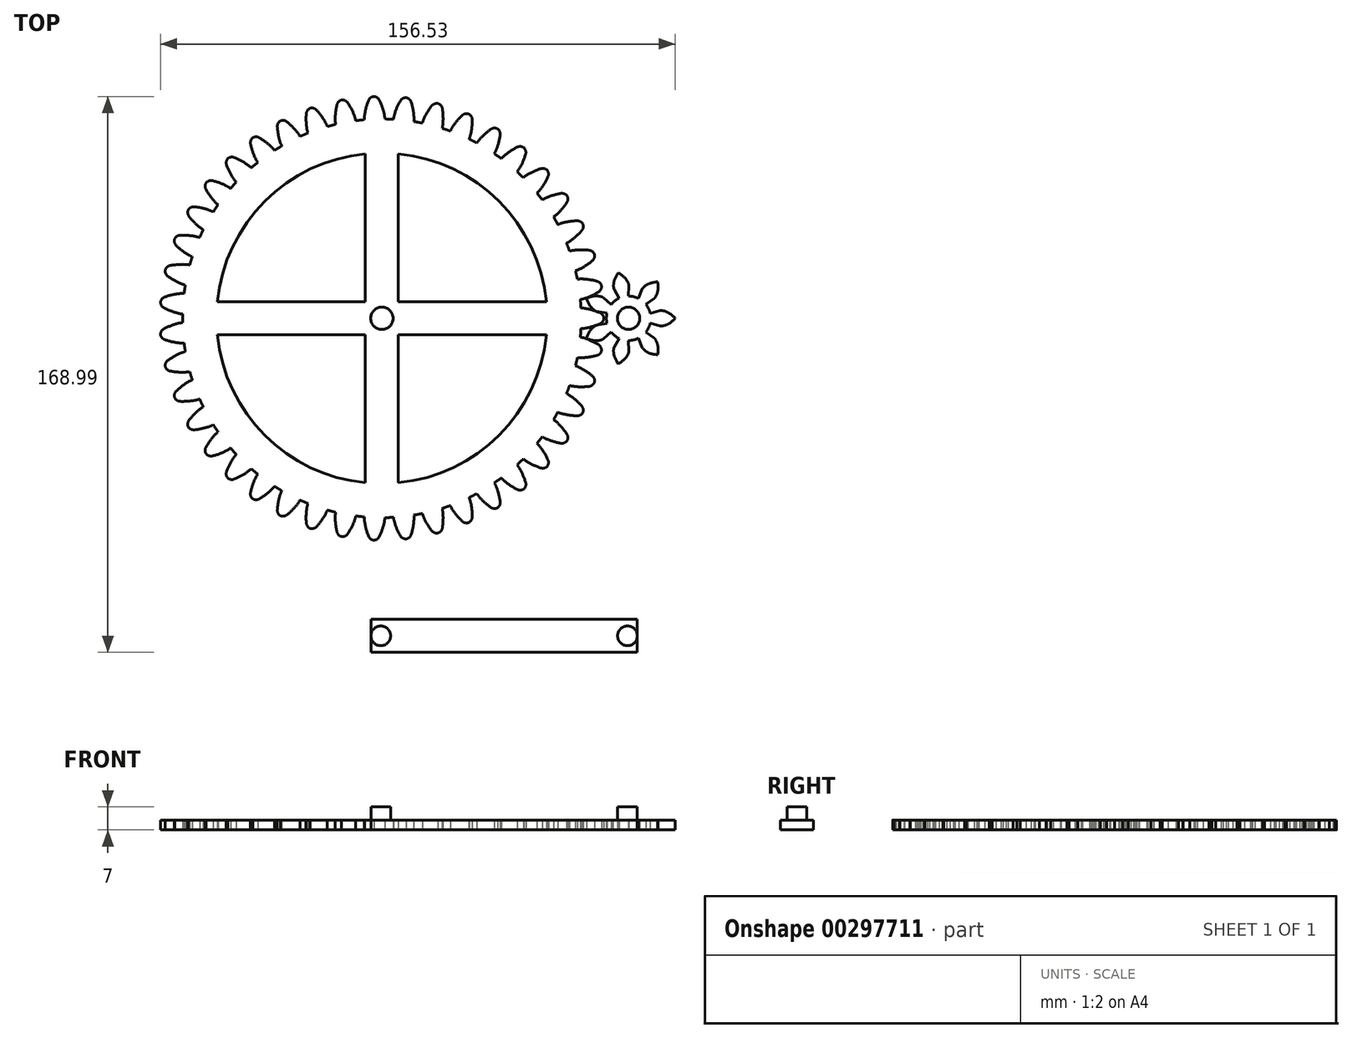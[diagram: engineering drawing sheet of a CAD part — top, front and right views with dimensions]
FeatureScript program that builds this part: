
annotation { "Feature Type Name" : "Feature", "Feature Type Description" : "" }
export const myFeature = defineFeature(function(context is Context, id is Id, definition is map)
    precondition{}
    {
        {
            var Q0;
            Q0=qCreatedBy(makeId("Top.planeOp"),FACE);
            var sketch = newSketch(context, id + "F0", { "sketchPlane" : qUnion([Q0])});
            skCircle(sketch, "E0", {"center": v(0, 0) * mm, "radius": 64.5 * mm, "construction": true});
            skLineSegment(sketch, "E1", {"start": v(0, 0) * mm, "end": v(75, 0) * mm, "construction": true});
            skCircle(sketch, "E2", {"center": v(75, 0) * mm, "radius": 10.5 * mm, "construction": true});
            skCircle(sketch, "E3", {"center": v(0, 0) * mm, "radius": 60.61 * mm, "construction": true});
            skCircle(sketch, "E4", {"center": v(75, 0) * mm, "radius": 6.75 * mm, "construction": true});
            skCircle(sketch, "E5", {"center": v(0, 0) * mm, "radius": 67.5 * mm, "construction": true});
            skCircle(sketch, "E6", {"center": v(75, 0) * mm, "radius": 13.5 * mm, "construction": true});
            skLineSegment(sketch, "E7", {"start": v(0, 0) * mm, "end": v(0, 64.5) * mm, "construction": true});
            skLineSegment(sketch, "E8", {"start": v(-20.73, 56.95) * mm, "end": v(20.73, 72.05) * mm});
            skLineSegment(sketch, "E9", {"start": v(0, 0) * mm, "end": v(-20.73, 56.95) * mm, "construction": true});
            skCircle(sketch, "E10", {"center": v(0, 0) * mm, "radius": 61.5 * mm, "construction": true});
            skLineSegment(sketch, "E11", {"start": v(-20.73, 56.95) * mm, "end": v(-20.73, 56.95) * mm});
            skArc(sketch, "E12", {"start": v(0.9, 60.6) * mm, "mid": v(-10.08, 59.77) * mm, "end": v(-20.73, 56.95) * mm});
            skLineSegment(sketch, "E13", {"start": v(-28.05, 53.73) * mm, "end": v(-1.4, 67.64) * mm});
            skArc(sketch, "E14", {"start": v(-28.05, 53.73) * mm, "mid": v(-24.44, 55.46) * mm, "end": v(-20.73, 56.95) * mm});
            skLineSegment(sketch, "E15", {"start": v(-10.08, 59.77) * mm, "end": v(0.8, 61.6) * mm});
            skArc(sketch, "E16", {"start": v(-10.08, 59.77) * mm, "mid": v(-4.6, 60.43) * mm, "end": v(0.9, 60.6) * mm});
            skLineSegment(sketch, "E17", {"start": v(-0.26, 65.19) * mm, "end": v(-22.54, 56.26) * mm});
            skArc(sketch, "E18", {"start": v(-22.54, 56.26) * mm, "mid": v(-11.03, 59.6) * mm, "end": v(0.9, 60.6) * mm});
            skSolve(sketch);
        }
        {
            var Q0;
            Q0=qCreatedBy(makeId("Top.planeOp"),FACE);
            var sketch = newSketch(context, id + "F1", { "sketchPlane" : qUnion([Q0])});
            skFitSpline(sketch, "E19", {"points": [v(-1.4, 67.64) * mm, v(0.9, 60.6) * mm], "startDerivative": vector(4.2, -7.99) * mm, "endDerivative": vector(0.2, -5.13) * mm});
            skPoint(sketch, "E20", {"position": v(-0.26, 65.19) * mm});
            skPoint(sketch, "E21", {"position": v(0, 64.5) * mm});
            skPoint(sketch, "E22", {"position": v(0.8, 61.6) * mm});
            skLineSegment(sketch, "E23", {"start": v(0, 0) * mm, "end": v(-2.47, 67.53) * mm, "construction": true});
            skFitSpline(sketch, "E24.MirrorCS", {"points": [v(-3.54, 67.56) * mm, v(-5.32, 60.38) * mm], "startDerivative": vector(-3.6, -8.27) * mm, "endDerivative": vector(0.18, -5.13) * mm});
            skArc(sketch, "E25", {"start": v(0, 64.5) * mm, "mid": v(-2.36, 64.46) * mm, "end": v(-4.7, 64.33) * mm, "construction": true});
            skArc(sketch, "E26", {"start": v(-5.32, 60.38) * mm, "mid": v(-2.21, 60.57) * mm, "end": v(0.9, 60.6) * mm});
            skArc(sketch, "E27", {"start": v(-3.61, 67.4) * mm, "mid": v(-2.47, 67.45) * mm, "end": v(-1.32, 67.49) * mm});
            skPoint(sketch, "E28", {"position": v(-3.61, 67.4) * mm});
            skSolve(sketch);
        }
        {
            var Q0;
            Q0=qCreatedBy(makeId("Top.planeOp"),FACE);
            var sketch = newSketch(context, id + "F2", { "sketchPlane" : qUnion([Q0])});
            skCircle(sketch, "E29", {"center": v(0, 0) * mm, "radius": 60.61 * mm});
            skCircle(sketch, "E30", {"center": v(0, 0) * mm, "radius": 3.4 * mm});
            skSolve(sketch);
        }
        {
            var Q0;
            Q0 = qSketchRegion(id + "F2", true);
            extrude(context, id + "F3", {"entities" : qUnion([Q0]), "depth" : 3 * mm});
        }
        {
            var Q0;
            Q0 = qSketchRegion(id + "F1", true);
            extrude(context, id + "F4", {"entities" : qUnion([Q0]), "depth" : 3 * mm});
        }
        {
            var Q0;
            Q0=makeQuery(id+"F4.opExtrude","SWEPT_EDGE",EDGE,{"disambiguationData":[OSD([sQuery(id+"F1.wireOp",EDGE,"E24.MirrorCS"),sQuery(id+"F1.wireOp",EDGE,"E27")])]});
            var Q1;
            Q1=makeQuery(id+"F4.opExtrude","SWEPT_EDGE",EDGE,{"disambiguationData":[OSD([sQuery(id+"F1.wireOp",EDGE,"E19"),sQuery(id+"F1.wireOp",EDGE,"E27")])]});
            fillet(context, id + "F5", {"entities" : qUnion([Q0, Q1]), "radius" : 2 * mm, "tangentPropagation" : true, "allowEdgeOverflow" : false});
        }
        {
            var Q0;
            Q0=makeQuery(id+"F4.opExtrude","SWEPT_BODY",BODY,{"disambiguationData":[OSD([sQuery(id+"F1.wireOp",EDGE,"E19"),sQuery(id+"F1.wireOp",EDGE,"g3GUBWuI-gOIz-DfBo-NTk1-D6WPWTrGzEXl"),sQuery(id+"F1.wireOp",EDGE,"E24.MirrorCS"),sQuery(id+"F1.wireOp",EDGE,"E26"),sQuery(id+"F1.wireOp",EDGE,"E27")])]});
            var Q1;
            Q1=sQuery(id+"F0.wireOp",EDGE,"E3");
            circularPattern(context, id + "F6", {"operationType" : NewBodyOperationType.ADD, "entities" : qUnion([Q0]), "axis" : qUnion([Q1]), "angle" : 360 * degree, "instanceCount" : 43, "equalSpace" : true});
        }
        {
            var Q0;
            Q0=qCreatedBy(makeId("Top.planeOp"),FACE);
            var sketch = newSketch(context, id + "F7", { "sketchPlane" : qUnion([Q0])});
            skLineSegment(sketch, "E31", {"start": v(75, 11.45) * mm, "end": v(75, -11.45) * mm, "construction": true});
            skPoint(sketch, "E32", {"position": v(75, 10.5) * mm});
            skLineSegment(sketch, "E33", {"start": v(71.63, 9.27) * mm, "end": v(77.76, 11.5) * mm});
            skArc(sketch, "E34", {"start": v(72.71, 9.6) * mm, "mid": v(73.92, 9.8) * mm, "end": v(75.15, 9.87) * mm});
            skArc(sketch, "E35", {"start": v(75.15, 9.87) * mm, "mid": v(73.36, 9.73) * mm, "end": v(71.63, 9.27) * mm});
            skArc(sketch, "E36", {"start": v(75.15, 9.87) * mm, "mid": v(74.24, 9.84) * mm, "end": v(73.34, 9.73) * mm});
            skLineSegment(sketch, "E37", {"start": v(75.13, 10.03) * mm, "end": v(73.34, 9.73) * mm});
            skArc(sketch, "E38", {"start": v(75.15, 9.87) * mm, "mid": v(72.96, 9.65) * mm, "end": v(70.88, 8.96) * mm});
            skLineSegment(sketch, "E39", {"start": v(70.88, 8.96) * mm, "end": v(74.87, 10.8) * mm});
            skArc(sketch, "E40", {"start": v(75.15, 9.87) * mm, "mid": v(72.16, 9.45) * mm, "end": v(69.43, 8.15) * mm});
            skLineSegment(sketch, "E41", {"start": v(69.43, 8.15) * mm, "end": v(74.44, 11.57) * mm});
            skArc(sketch, "E42", {"start": v(75.15, 9.87) * mm, "mid": v(71.32, 9.16) * mm, "end": v(68.07, 7.02) * mm});
            skLineSegment(sketch, "E43", {"start": v(68.07, 7.02) * mm, "end": v(73.64, 12.52) * mm});
            skArc(sketch, "E44", {"start": v(75.15, 9.87) * mm, "mid": v(69.9, 8.45) * mm, "end": v(66.2, 4.48) * mm});
            skLineSegment(sketch, "E45", {"start": v(66.2, 4.48) * mm, "end": v(71.2, 14.28) * mm});
            skCircle(sketch, "E46", {"center": v(75, 0) * mm, "radius": 9.87 * mm, "construction": true});
            skSolve(sketch);
        }
        {
            var Q0;
            Q0=qCreatedBy(makeId("Top.planeOp"),FACE);
            var sketch = newSketch(context, id + "F8", { "sketchPlane" : qUnion([Q0])});
            skLineSegment(sketch, "E47.bottom", {"start": v(-3.34, -91.54) * mm, "end": v(77.66, -91.54) * mm});
            skLineSegment(sketch, "E47.top", {"start": v(-3.34, -101.54) * mm, "end": v(77.66, -101.54) * mm});
            skLineSegment(sketch, "E47.left", {"start": v(-3.34, -91.54) * mm, "end": v(-3.34, -101.54) * mm});
            skLineSegment(sketch, "E47.right", {"start": v(77.66, -91.54) * mm, "end": v(77.66, -101.54) * mm});
            skSolve(sketch);
        }
        {
            var Q0;
            Q0 = qSketchRegion(id + "F8", true);
            extrude(context, id + "F9", {"entities" : qUnion([Q0]), "depth" : 3 * mm});
        }
        {
            var Q0;
            Q0=qCreatedBy(makeId("Top.planeOp"),FACE);
            var sketch = newSketch(context, id + "F10", { "sketchPlane" : qUnion([Q0])});
            skCircle(sketch, "E48", {"center": v(75, 0) * mm, "radius": 6.75 * mm});
            skCircle(sketch, "E49", {"center": v(75, 0) * mm, "radius": 3.4 * mm});
            skSolve(sketch);
        }
        {
            var Q0;
            Q0 = qSketchRegion(id + "F10", true);
            extrude(context, id + "F11", {"entities" : qUnion([Q0]), "depth" : 3 * mm});
        }
        {
            var Q0;
            Q0=makeQuery(id+"F11.opExtrude","SWEPT_BODY",BODY,{"disambiguationData":[OSD([sQuery(id+"F10.wireOp",EDGE,"E48"),sQuery(id+"F10.wireOp",EDGE,"E49")])]});
            var Q1;
            Q1=sQuery(id+"F0.wireOp",EDGE,"E4");
            transform(context, id + "F12", {"entities" : qUnion([Q0]), "transformType" : TransformType.ROTATION, "transformAxis" : qUnion([Q1]), "angle" : 24 * degree, "makeCopy" : false});
        }
        {
            var Q0;
            Q0=qCreatedBy(makeId("Top.planeOp"),FACE);
            var sketch = newSketch(context, id + "F13", { "sketchPlane" : qUnion([Q0])});
            skLineSegment(sketch, "E50", {"start": v(75, 0) * mm, "end": v(72.66, 10.24) * mm, "construction": true});
            skLineSegment(sketch, "E51", {"start": v(75.13, 10.03) * mm, "end": v(74.95, 6.75) * mm});
            skLineSegment(sketch, "E52.MirrorCS", {"start": v(70.53, 8.98) * mm, "end": v(72.12, 6.1) * mm});
            skArc(sketch, "E53", {"start": v(72.12, 6.1) * mm, "mid": v(73.5, 6.58) * mm, "end": v(74.95, 6.75) * mm});
            skFitSpline(sketch, "E54", {"points": [v(75.13, 10.03) * mm, v(74.87, 10.8) * mm, v(74.44, 11.57) * mm, v(73.64, 12.52) * mm, v(71.2, 14.28) * mm], "startDerivative": vector(-0.18, 1.81) * mm, "endDerivative": vector(-6.13, 3.97) * mm});
            skFitSpline(sketch, "E55.MirrorCS", {"points": [v(70.53, 8.98) * mm, v(70.43, 9.79) * mm, v(70.49, 10.66) * mm, v(70.79, 11.87) * mm, v(72.23, 14.52) * mm], "startDerivative": vector(-0.62, 1.71) * mm, "endDerivative": vector(3.8, 6.23) * mm});
            skSolve(sketch);
        }
        {
            var Q0;
            {var subQ1=sQuery(id+"F13.wireOp",EDGE,"E51");Q0=makeQuery(id+"F13.imprint","IMPRINT",FACE,{"disambiguationData":[TD([[makeQuery(id+"F13.imprint","IMPRINT",EDGE,{"derivedFrom":subQ1}),-1.0]])]});}
            extrude(context, id + "F14", {"entities" : qUnion([Q0]), "depth" : 3 * mm});
        }
        {
            var Q0;
            Q0=makeQuery(id+"F14.opExtrude","SWEPT_EDGE",EDGE,{"disambiguationData":[OSD([sQuery(id+"F13.wireOp",EDGE,"E52.MirrorCS"),sQuery(id+"F13.wireOp",EDGE,"E55.MirrorCS")])]});
            var Q1;
            Q1=makeQuery(id+"F14.opExtrude","SWEPT_EDGE",EDGE,{"disambiguationData":[OSD([sQuery(id+"F13.wireOp",EDGE,"E51"),sQuery(id+"F13.wireOp",EDGE,"E54")])]});
            fillet(context, id + "F15", {"entities" : qUnion([Q0, Q1]), "radius" : 1 * mm, "tangentPropagation" : true, "allowEdgeOverflow" : false});
        }
        {
            var Q0;
            Q0=makeQuery(id+"F14.opExtrude","SWEPT_BODY",BODY,{"disambiguationData":[OSD([sQuery(id+"F13.wireOp",EDGE,"35af973c-5e85-4642-a154-4425b26c4466"),sQuery(id+"F13.wireOp",EDGE,"5fb0300e-90d4-42b1-9b06-9f1f845147b70.MirrorCS"),sQuery(id+"F13.wireOp",EDGE,"E51"),sQuery(id+"F13.wireOp",EDGE,"E52.MirrorCS"),sQuery(id+"F13.wireOp",EDGE,"E53"),sQuery(id+"F13.wireOp",EDGE,"hAwYp26g-f9RW-9ect-Whx0-MuxyCeAYNdfw")])]});
            var Q1;
            Q1=makeQuery(id+"F11.opExtrude","CAP_EDGE",EDGE,{"disambiguationData":[OSD([sQuery(id+"F10.wireOp",EDGE,"E48")])],"isStart":false});
            circularPattern(context, id + "F16", {"operationType" : NewBodyOperationType.ADD, "entities" : qUnion([Q0]), "axis" : qUnion([Q1]), "angle" : 360 * degree, "instanceCount" : 7, "equalSpace" : true});
        }
        {
            var Q0;
            Q0=makeQuery(id+"F9.opExtrude","CAP_FACE",FACE,{"disambiguationData":[OSD([sQuery(id+"F8.wireOp",EDGE,"E47.bottom"),sQuery(id+"F8.wireOp",EDGE,"E47.top"),sQuery(id+"F8.wireOp",EDGE,"E47.left"),sQuery(id+"F8.wireOp",EDGE,"E47.right")])],"isStart":false});
            var sketch = newSketch(context, id + "F17", { "sketchPlane" : qUnion([Q0])});
            skLineSegment(sketch, "E56", {"start": v(-0.34, -96.54) * mm, "end": v(74.66, -96.54) * mm, "construction": true});
            skCircle(sketch, "E57", {"center": v(-0.34, -96.54) * mm, "radius": 3 * mm});
            skCircle(sketch, "E58", {"center": v(74.66, -96.54) * mm, "radius": 3 * mm});
            skSolve(sketch);
        }
        {
            var Q0;
            Q0 = qSketchRegion(id + "F17", true);
            extrude(context, id + "F18", {"entities" : qUnion([Q0]), "operationType" : NewBodyOperationType.ADD, "depth" : 4 * mm});
        }
        {
            var Q0;
            Q0=qCreatedBy(makeId("Top.planeOp"),FACE);
            var sketch = newSketch(context, id + "F19", { "sketchPlane" : qUnion([Q0])});
            skLineSegment(sketch, "E59", {"start": v(5, 50) * mm, "end": v(5, 5) * mm});
            skLineSegment(sketch, "E60", {"start": v(5, 5) * mm, "end": v(50, 5) * mm});
            skArc(sketch, "E61", {"start": v(50, 5) * mm, "mid": v(35.58, 35.58) * mm, "end": v(5, 50) * mm});
            skLineSegment(sketch, "E62.1.0", {"start": v(-50, 5) * mm, "end": v(-5, 5) * mm});
            skArc(sketch, "E62.1.1", {"start": v(-5, 50) * mm, "mid": v(-35.58, 35.58) * mm, "end": v(-50, 5) * mm});
            skLineSegment(sketch, "E62.1.2", {"start": v(-5, 5) * mm, "end": v(-5, 50) * mm});
            skLineSegment(sketch, "E62.2.0", {"start": v(-5, -50) * mm, "end": v(-5, -5) * mm});
            skArc(sketch, "E62.2.1", {"start": v(-50, -5) * mm, "mid": v(-35.58, -35.58) * mm, "end": v(-5, -50) * mm});
            skLineSegment(sketch, "E62.2.2", {"start": v(-5, -5) * mm, "end": v(-50, -5) * mm});
            skLineSegment(sketch, "E62.3.0", {"start": v(50, -5) * mm, "end": v(5, -5) * mm});
            skArc(sketch, "E62.3.1", {"start": v(5, -50) * mm, "mid": v(35.58, -35.58) * mm, "end": v(50, -5) * mm});
            skLineSegment(sketch, "E62.3.2", {"start": v(5, -5) * mm, "end": v(5, -50) * mm});
            skPoint(sketch, "E62.center", {"position": v(0, 0) * mm});
            skSolve(sketch);
        }
        {
            var Q0;
            Q0 = qSketchRegion(id + "F19", true);
            extrude(context, id + "F20", {"entities" : qUnion([Q0]), "operationType" : NewBodyOperationType.REMOVE, "depth" : 25 * mm});
        }
    });
